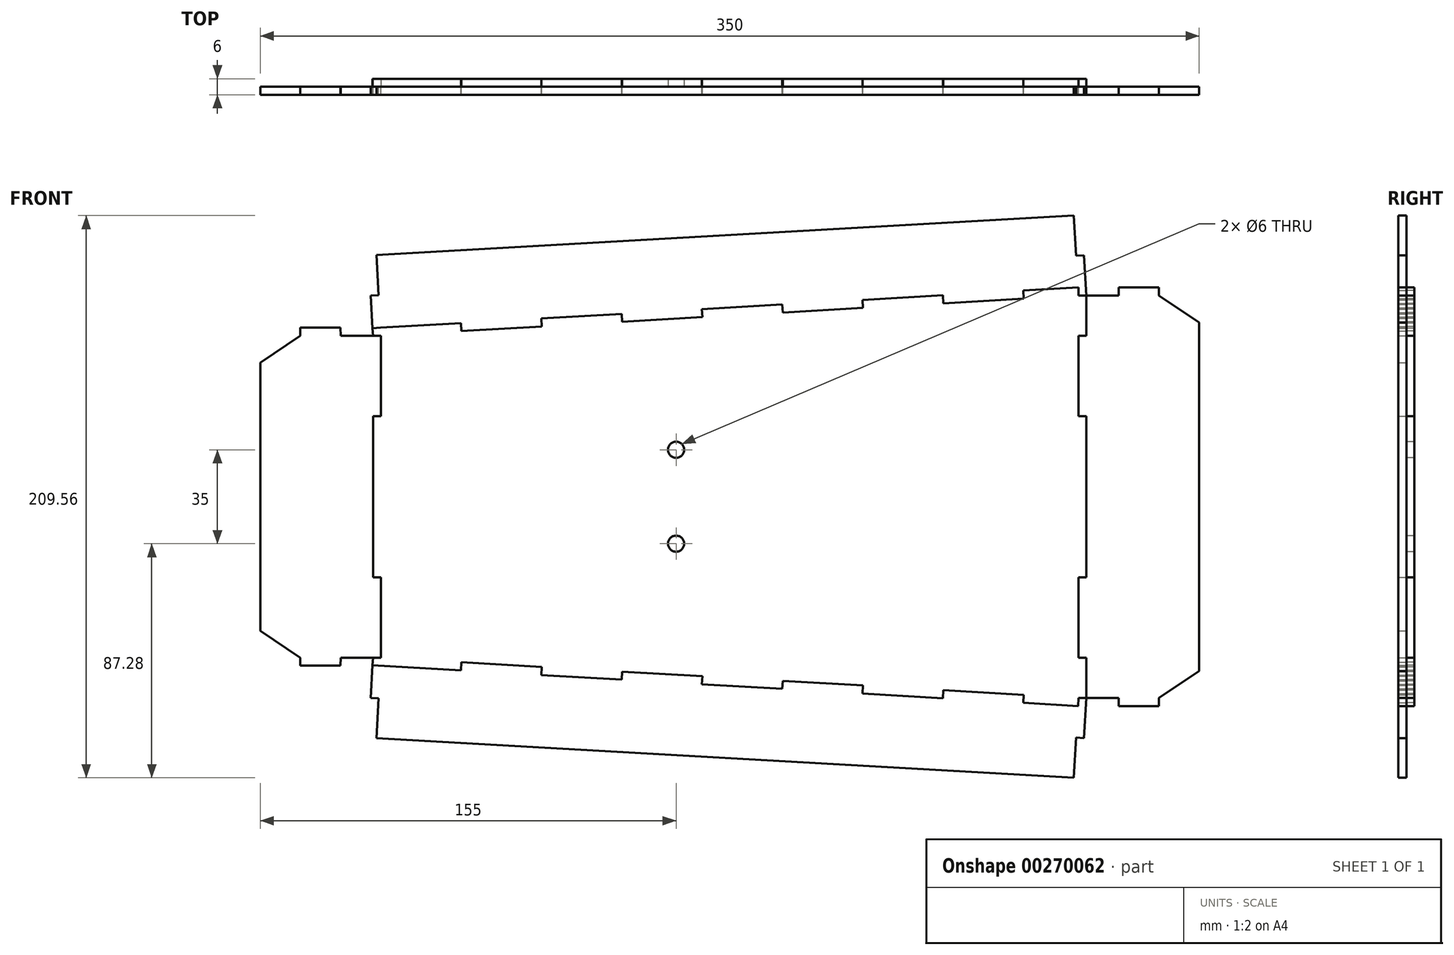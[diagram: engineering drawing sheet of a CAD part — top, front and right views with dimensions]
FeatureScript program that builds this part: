
annotation { "Feature Type Name" : "Feature", "Feature Type Description" : "" }
export const myFeature = defineFeature(function(context is Context, id is Id, definition is map)
    precondition{}
    {
        {
            var Q0;
            Q0=qCreatedBy(makeId("Front.planeOp"),FACE);
            var sketch = newSketch(context, id + "F0", { "sketchPlane" : qUnion([Q0])});
            skLineSegment(sketch, "E0", {"start": v(0, 0) * mm, "end": v(-130, 0) * mm, "construction": true});
            skLineSegment(sketch, "E1", {"start": v(0, 0) * mm, "end": v(130, 0) * mm, "construction": true});
            skLineSegment(sketch, "E2", {"start": v(130, 0) * mm, "end": v(130, 75) * mm, "construction": true});
            skLineSegment(sketch, "E3", {"start": v(-130, 0) * mm, "end": v(-130, 60) * mm, "construction": true});
            skLineSegment(sketch, "E4", {"start": v(-130, 60) * mm, "end": v(130, 75) * mm, "construction": true});
            skLineSegment(sketch, "E5.0", {"start": v(-133, 0) * mm, "end": v(-133, 60) * mm, "construction": true});
            skLineSegment(sketch, "E6.0", {"start": v(133, 0) * mm, "end": v(133, 75) * mm, "construction": true});
            skLineSegment(sketch, "E7", {"start": v(-100.22, 64.73) * mm, "end": v(-130.17, 63) * mm});
            skLineSegment(sketch, "E8", {"start": v(-100.22, 64.73) * mm, "end": v(-100.05, 61.73) * mm});
            skLineSegment(sketch, "E9", {"start": v(-100.05, 61.73) * mm, "end": v(-70.1, 63.46) * mm});
            skLineSegment(sketch, "E10", {"start": v(-70.1, 63.46) * mm, "end": v(-70.27, 66.45) * mm});
            skLineSegment(sketch, "E11", {"start": v(-70.27, 66.45) * mm, "end": v(-40.32, 68.18) * mm});
            skLineSegment(sketch, "E12", {"start": v(-40.32, 68.18) * mm, "end": v(-40.15, 65.18) * mm});
            skLineSegment(sketch, "E13", {"start": v(-40.15, 65.18) * mm, "end": v(-10.2, 66.91) * mm});
            skLineSegment(sketch, "E14", {"start": v(-10.2, 66.91) * mm, "end": v(-10.37, 69.9) * mm});
            skLineSegment(sketch, "E15", {"start": v(-10.37, 69.9) * mm, "end": v(19.58, 71.63) * mm});
            skLineSegment(sketch, "E16", {"start": v(19.58, 71.63) * mm, "end": v(19.75, 68.64) * mm});
            skLineSegment(sketch, "E17", {"start": v(19.75, 68.64) * mm, "end": v(49.7, 70.37) * mm});
            skLineSegment(sketch, "E18", {"start": v(49.7, 70.37) * mm, "end": v(49.53, 73.36) * mm});
            skLineSegment(sketch, "E19", {"start": v(49.53, 73.36) * mm, "end": v(79.48, 75.1) * mm});
            skLineSegment(sketch, "E20", {"start": v(79.48, 75.1) * mm, "end": v(79.65, 72.1) * mm});
            skLineSegment(sketch, "E21", {"start": v(79.65, 72.1) * mm, "end": v(109.6, 73.82) * mm});
            skLineSegment(sketch, "E22", {"start": v(129.15, 89.8) * mm, "end": v(128.28, 104.78) * mm});
            skLineSegment(sketch, "E23", {"start": v(-131.74, 90.13) * mm, "end": v(-130.88, 75.15) * mm});
            skLineSegment(sketch, "E24", {"start": v(-130, 0) * mm, "end": v(-133, 0) * mm});
            skLineSegment(sketch, "E25", {"start": v(-133, 0) * mm, "end": v(-133, 30) * mm});
            skLineSegment(sketch, "E26", {"start": v(-133, 30) * mm, "end": v(-130, 30) * mm});
            skLineSegment(sketch, "E27", {"start": v(-130, 30) * mm, "end": v(-130, 60) * mm});
            skLineSegment(sketch, "E28", {"start": v(130, 0) * mm, "end": v(133, 0) * mm});
            skLineSegment(sketch, "E29", {"start": v(133, 0) * mm, "end": v(133, 30) * mm});
            skLineSegment(sketch, "E30", {"start": v(133, 30) * mm, "end": v(130, 30) * mm});
            skLineSegment(sketch, "E31", {"start": v(130, 30) * mm, "end": v(130, 60) * mm});
            skLineSegment(sketch, "E32", {"start": v(130, 60) * mm, "end": v(133, 60) * mm});
            skLineSegment(sketch, "E33", {"start": v(133, 60) * mm, "end": v(133, 75) * mm});
            skLineSegment(sketch, "E34", {"start": v(130, 75) * mm, "end": v(133, 75) * mm});
            skLineSegment(sketch, "E35.0", {"start": v(175, 0) * mm, "end": v(175, 65) * mm});
            skLineSegment(sketch, "E36.0", {"start": v(-175, 0) * mm, "end": v(-175, 50) * mm});
            skLineSegment(sketch, "E37", {"start": v(-130, 60) * mm, "end": v(-145, 60) * mm});
            skLineSegment(sketch, "E38", {"start": v(-145, 60) * mm, "end": v(-145.17, 63) * mm});
            skLineSegment(sketch, "E39", {"start": v(-145.17, 63) * mm, "end": v(-160.17, 63) * mm});
            skLineSegment(sketch, "E40", {"start": v(-160.17, 63) * mm, "end": v(-160.17, 60) * mm});
            skLineSegment(sketch, "E41.trimOffspring", {"start": v(-145, 60) * mm, "end": v(-130, 60) * mm});
            skLineSegment(sketch, "E42", {"start": v(-133.34, 65.75) * mm, "end": v(-133, 60) * mm});
            skLineSegment(sketch, "E43", {"start": v(-133, 60) * mm, "end": v(-133.87, 74.97) * mm});
            skLineSegment(sketch, "E44", {"start": v(-133.87, 74.97) * mm, "end": v(-130.88, 75.15) * mm});
            skLineSegment(sketch, "E45", {"start": v(-130.88, 75.15) * mm, "end": v(-131.74, 90.13) * mm});
            skLineSegment(sketch, "E46.trimOffspring", {"start": v(-133.87, 74.97) * mm, "end": v(-133.34, 65.75) * mm});
            skLineSegment(sketch, "E47.0", {"start": v(132.91, 76.58) * mm, "end": v(132.14, 89.98) * mm});
            skLineSegment(sketch, "E48", {"start": v(133, 75) * mm, "end": v(132.91, 76.58) * mm});
            skLineSegment(sketch, "E49", {"start": v(133, 75) * mm, "end": v(132.14, 89.98) * mm});
            skLineSegment(sketch, "E50", {"start": v(132.14, 89.98) * mm, "end": v(129.15, 89.8) * mm});
            skLineSegment(sketch, "E51", {"start": v(133, 75) * mm, "end": v(145, 75) * mm});
            skLineSegment(sketch, "E52", {"start": v(130, 75) * mm, "end": v(145, 75) * mm});
            skLineSegment(sketch, "E53", {"start": v(145, 75) * mm, "end": v(145, 78) * mm});
            skLineSegment(sketch, "E54", {"start": v(145, 78) * mm, "end": v(160, 78) * mm});
            skLineSegment(sketch, "E55", {"start": v(160, 78) * mm, "end": v(160, 75) * mm});
            skLineSegment(sketch, "E56", {"start": v(-175, 0) * mm, "end": v(175, 0) * mm, "construction": true});
            skLineSegment(sketch, "E57.MirrorCS", {"start": v(133, -75) * mm, "end": v(132.91, -76.58) * mm});
            skLineSegment(sketch, "E58.MirrorCS", {"start": v(130, -75) * mm, "end": v(133, -75) * mm});
            skLineSegment(sketch, "E59.MirrorCS", {"start": v(-133.34, -65.75) * mm, "end": v(-133, -60) * mm});
            skLineSegment(sketch, "E60.MirrorCS", {"start": v(-133.87, -74.97) * mm, "end": v(-130.88, -75.15) * mm});
            skLineSegment(sketch, "E61.MirrorCS", {"start": v(-130, -60) * mm, "end": v(-145, -60) * mm});
            skLineSegment(sketch, "E62.MirrorCS", {"start": v(-133.87, -74.97) * mm, "end": v(-133.34, -65.75) * mm});
            skLineSegment(sketch, "E63.MirrorCS", {"start": v(129.15, -89.8) * mm, "end": v(128.28, -104.78) * mm});
            skLineSegment(sketch, "E64.MirrorCS", {"start": v(-133, -60) * mm, "end": v(-133.87, -74.97) * mm});
            skLineSegment(sketch, "E65.MirrorCS", {"start": v(-145, -60) * mm, "end": v(-130, -60) * mm});
            skLineSegment(sketch, "E66.MirrorCS", {"start": v(-130.88, -75.15) * mm, "end": v(-131.73, -89.95) * mm});
            skLineSegment(sketch, "E67.MirrorCS", {"start": v(132.14, -89.98) * mm, "end": v(129.15, -89.8) * mm});
            skLineSegment(sketch, "E68.MirrorCS", {"start": v(-145, -60) * mm, "end": v(-145.17, -63) * mm});
            skLineSegment(sketch, "E69.MirrorCS", {"start": v(133, -75) * mm, "end": v(132.14, -89.98) * mm});
            skLineSegment(sketch, "E70.MirrorCS", {"start": v(133, -75) * mm, "end": v(145, -75) * mm});
            skLineSegment(sketch, "E71.MirrorCS", {"start": v(132.91, -76.58) * mm, "end": v(132.14, -89.98) * mm});
            skLineSegment(sketch, "E72.MirrorCS", {"start": v(160, -78) * mm, "end": v(160, -75) * mm});
            skLineSegment(sketch, "E73.MirrorCS", {"start": v(130, -75) * mm, "end": v(145, -75) * mm});
            skLineSegment(sketch, "E74.MirrorCS", {"start": v(-131.73, -89.95) * mm, "end": v(-130.88, -75.15) * mm});
            skLineSegment(sketch, "E75.MirrorCS", {"start": v(-160.17, -63) * mm, "end": v(-160.17, -60) * mm});
            skLineSegment(sketch, "E76.MirrorCS", {"start": v(145, -75) * mm, "end": v(145, -78) * mm});
            skLineSegment(sketch, "E77.MirrorCS", {"start": v(49.7, -70.37) * mm, "end": v(49.53, -73.36) * mm});
            skLineSegment(sketch, "E78.MirrorCS", {"start": v(133, -30) * mm, "end": v(130, -30) * mm});
            skLineSegment(sketch, "E79.MirrorCS", {"start": v(-40.32, -68.18) * mm, "end": v(-40.15, -65.18) * mm});
            skLineSegment(sketch, "E80.MirrorCS", {"start": v(-133, -30) * mm, "end": v(-130, -30) * mm});
            skLineSegment(sketch, "E81.MirrorCS", {"start": v(133, -60) * mm, "end": v(133, -75) * mm});
            skLineSegment(sketch, "E82.MirrorCS", {"start": v(145, -78) * mm, "end": v(160, -78) * mm});
            skLineSegment(sketch, "E83.MirrorCS", {"start": v(-10.2, -66.91) * mm, "end": v(-10.37, -69.9) * mm});
            skLineSegment(sketch, "E84.MirrorCS", {"start": v(-145.17, -63) * mm, "end": v(-160.17, -63) * mm});
            skLineSegment(sketch, "E85.MirrorCS", {"start": v(130, -60) * mm, "end": v(133, -60) * mm});
            skLineSegment(sketch, "E86.MirrorCS", {"start": v(19.58, -71.63) * mm, "end": v(19.75, -68.64) * mm});
            skLineSegment(sketch, "E87.MirrorCS", {"start": v(79.48, -75.1) * mm, "end": v(79.65, -72.1) * mm});
            skLineSegment(sketch, "E88.MirrorCS", {"start": v(-70.1, -63.46) * mm, "end": v(-70.27, -66.45) * mm});
            skLineSegment(sketch, "E89.MirrorCS", {"start": v(-100.22, -64.73) * mm, "end": v(-100.05, -61.73) * mm});
            skLineSegment(sketch, "E90.MirrorCS", {"start": v(133, 0) * mm, "end": v(133, -30) * mm});
            skLineSegment(sketch, "E91.MirrorCS", {"start": v(19.75, -68.64) * mm, "end": v(49.7, -70.37) * mm});
            skLineSegment(sketch, "E92.MirrorCS", {"start": v(79.65, -72.1) * mm, "end": v(109.6, -73.82) * mm});
            skLineSegment(sketch, "E93.MirrorCS", {"start": v(-40.15, -65.18) * mm, "end": v(-10.2, -66.91) * mm});
            skLineSegment(sketch, "E94.MirrorCS", {"start": v(130, 0) * mm, "end": v(130, -75) * mm, "construction": true});
            skLineSegment(sketch, "E95.MirrorCS", {"start": v(130, -30) * mm, "end": v(130, -60) * mm});
            skLineSegment(sketch, "E96.MirrorCS", {"start": v(-10.37, -69.9) * mm, "end": v(19.58, -71.63) * mm});
            skLineSegment(sketch, "E97.MirrorCS", {"start": v(49.53, -73.36) * mm, "end": v(79.48, -75.1) * mm});
            skLineSegment(sketch, "E98.MirrorCS", {"start": v(-70.27, -66.45) * mm, "end": v(-40.32, -68.18) * mm});
            skLineSegment(sketch, "E99.MirrorCS", {"start": v(-100.22, -64.73) * mm, "end": v(-133.17, -62.83) * mm});
            skLineSegment(sketch, "E100.MirrorCS", {"start": v(-133, 0) * mm, "end": v(-133, -30) * mm});
            skLineSegment(sketch, "E101.MirrorCS", {"start": v(-100.05, -61.73) * mm, "end": v(-70.1, -63.46) * mm});
            skLineSegment(sketch, "E102.MirrorCS", {"start": v(-175, 0) * mm, "end": v(-175, -50) * mm});
            skLineSegment(sketch, "E103.MirrorCS", {"start": v(-130, -30) * mm, "end": v(-130, -60) * mm});
            skLineSegment(sketch, "E104.MirrorCS", {"start": v(-130, -60) * mm, "end": v(130, -75) * mm, "construction": true});
            skLineSegment(sketch, "E105.MirrorCS", {"start": v(-133, 0) * mm, "end": v(-133, -60) * mm, "construction": true});
            skLineSegment(sketch, "E106.MirrorCS", {"start": v(-130, 0) * mm, "end": v(-130, -60) * mm, "construction": true});
            skLineSegment(sketch, "E107.MirrorCS", {"start": v(133, 0) * mm, "end": v(133, -75) * mm, "construction": true});
            skLineSegment(sketch, "E108.MirrorCS", {"start": v(175, 0) * mm, "end": v(175, -65) * mm});
            skPoint(sketch, "E109.orphan", {"position": v(-131.73, -89.95) * mm});
            skLineSegment(sketch, "E110", {"start": v(109.6, 73.82) * mm, "end": v(109.43, 76.82) * mm});
            skLineSegment(sketch, "E111", {"start": v(109.43, 76.82) * mm, "end": v(130.02, 78) * mm});
            skLineSegment(sketch, "E112", {"start": v(130.02, 78) * mm, "end": v(130, 75) * mm});
            skLineSegment(sketch, "E113", {"start": v(109.6, -73.82) * mm, "end": v(109.43, -76.82) * mm});
            skLineSegment(sketch, "E114", {"start": v(109.43, -76.82) * mm, "end": v(129.92, -78) * mm});
            skLineSegment(sketch, "E115", {"start": v(129.92, -78) * mm, "end": v(130, -75) * mm});
            skLineSegment(sketch, "E116", {"start": v(-130.17, 63) * mm, "end": v(-133.16, 62.83) * mm});
            skPoint(sketch, "E117.MirrorCS.end.orphan", {"position": v(130.5, -118.51) * mm});
            skPoint(sketch, "E118.MirrorCS.end.orphan", {"position": v(130.41, -119.93) * mm});
            skPoint(sketch, "E119.MirrorCS.end.orphan", {"position": v(131.28, -104.95) * mm});
            skPoint(sketch, "E120.MirrorCS.start.orphan", {"position": v(-135.6, -104.93) * mm});
            skPoint(sketch, "E121.MirrorCS.end.orphan", {"position": v(-134.73, -89.95) * mm});
            skLineSegment(sketch, "E122", {"start": v(128.28, 104.78) * mm, "end": v(-131.74, 90.13) * mm});
            skLineSegment(sketch, "E123", {"start": v(128.28, -104.78) * mm, "end": v(-131.73, -89.95) * mm});
            skLineSegment(sketch, "E124", {"start": v(0, 0) * mm, "end": v(0, 30) * mm, "construction": true});
            skLineSegment(sketch, "E125.0", {"start": v(-20, 0) * mm, "end": v(-20, 30) * mm, "construction": true});
            skCircle(sketch, "E126", {"center": v(-20, 17.5) * mm, "radius": 3 * mm});
            skCircle(sketch, "E127.MirrorC", {"center": v(-20, -17.5) * mm, "radius": 3 * mm});
            skLineSegment(sketch, "E128", {"start": v(-175, -50) * mm, "end": v(-160.17, -60) * mm});
            skPoint(sketch, "E129.start.orphan", {"position": v(-175, -60) * mm});
            skLineSegment(sketch, "E130", {"start": v(-175, 50) * mm, "end": v(-160.17, 60) * mm});
            skPoint(sketch, "E131.start.orphan", {"position": v(-175, 60) * mm});
            skLineSegment(sketch, "E132", {"start": v(175, 65) * mm, "end": v(160, 75) * mm});
            skPoint(sketch, "E133.orphan", {"position": v(175, 75) * mm});
            skLineSegment(sketch, "E134", {"start": v(175, -65) * mm, "end": v(160, -75.07) * mm});
            skPoint(sketch, "E135.MirrorCS.end.orphan", {"position": v(175, -75) * mm});
            skPoint(sketch, "E136.orphan", {"position": v(-131.74, -90.13) * mm});
            skPoint(sketch, "E137.end.orphan", {"position": v(129.92, 76.4) * mm});
            skPoint(sketch, "E138.MirrorCS.end.orphan", {"position": v(129.92, -76.4) * mm});
            skSolve(sketch);
        }
        {
            var Q0;
            Q0=makeQuery(id+"F0.imprint","IMPRINT",FACE,{"disambiguationData":[TD([[makeQuery(id+"F0.imprint","IMPRINT",EDGE,{"derivedFrom":sQuery(id+"F0.wireOp",EDGE,"E7")}),1.0]])]});
            extrude(context, id + "F1", {"entities" : qUnion([Q0]), "oppositeDirection" : true, "depth" : 3 * mm, "offsetDistance" : 25 * mm});
        }
        {
            var Q0;
            Q0=makeQuery(id+"F0.imprint","IMPRINT",FACE,{"disambiguationData":[TD([[makeQuery(id+"F0.imprint","IMPRINT",EDGE,{"derivedFrom":sQuery(id+"F0.wireOp",EDGE,"E7")}),-1.0]])]});
            extrude(context, id + "F2", {"entities" : qUnion([Q0]), "operationType" : NewBodyOperationType.ADD, "depth" : 3 * mm, "offsetDistance" : 25 * mm});
        }
        {
            var Q0;
            Q0=makeQuery(id+"F0.imprint","IMPRINT",FACE,{"disambiguationData":[TD([[makeQuery(id+"F0.imprint","IMPRINT",EDGE,{"derivedFrom":sQuery(id+"F0.wireOp",EDGE,"E25")}),1.0]])]});
            extrude(context, id + "F3", {"entities" : qUnion([Q0]), "operationType" : NewBodyOperationType.ADD, "depth" : 3 * mm, "offsetDistance" : 25 * mm});
        }
        {
            var Q0;
            {var subQ4=sQuery(id+"F0.wireOp",EDGE,"E60.MirrorCS");Q0=makeQuery(id+"F0.imprint","IMPRINT",FACE,{"disambiguationData":[TD([[makeQuery(id+"F0.imprint","IMPRINT",EDGE,{"derivedFrom":subQ4}),1.0]])]});}
            extrude(context, id + "F4", {"entities" : qUnion([Q0]), "operationType" : NewBodyOperationType.ADD, "depth" : 3 * mm, "offsetDistance" : 25 * mm});
        }
        {
            var Q0;
            Q0=makeQuery(id+"F0.imprint","IMPRINT",FACE,{"disambiguationData":[TD([[makeQuery(id+"F0.imprint","IMPRINT",EDGE,{"derivedFrom":sQuery(id+"F0.wireOp",EDGE,"E29")}),-1.0]])]});
            extrude(context, id + "F5", {"entities" : qUnion([Q0]), "operationType" : NewBodyOperationType.ADD, "depth" : 3 * mm, "offsetDistance" : 25 * mm});
        }
    });
